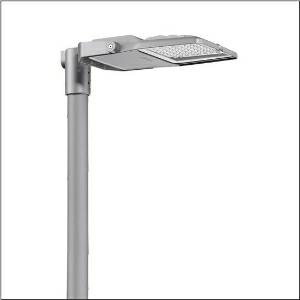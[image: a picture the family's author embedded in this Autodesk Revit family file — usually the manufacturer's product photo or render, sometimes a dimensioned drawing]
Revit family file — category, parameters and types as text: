
# Revit family: floodlight_fl_21_mini___pl52_5xa7776d2d3a_85e1
name_source: partatom
category: Lighting Fixtures
units: mm (PartAtom-declared; Revit-internal decimal feet)

## family parameters
Cut with Voids When Loaded = No
Host = Face
Light Source = No
Part Type = Normal
Room Calculation Point = No
Round Connector Dimension = Use Diameter
Shared = No

## types (1)
- --- (1 x LED, 17840 lm, 142.9 W, 3000K)
    Apparent Load = 143 VA
    CIE Flux Codes = 26 60 98 100 100
    Color Rendering = 70
    Color Temperature = 3000K
    Default Elevation = 1800 mm
    Description = Floodlight FL 21 mini, floodlight, primary light control with lens, of PMMA, primary optical cover: protective disc, of toughened safety glass, transparent, light distribution: PL52, light emission: direct distribution, installation type: surface-mounted, LED, High Power LED, rated luminous flux: 17.840lm, luminous efficacy: 125lm/W, light colour: 730, colour temperature: 3000K, control gear: Smart Interface (Zhaga), control: flexible luminous flux parameterisation, time-dependent luminous flux control, constant luminous flux control, overheat protection, pre-setting: logarithmic dimming characteristic, with terminal, 6-pole, mains connection: 220..240V, AC, 50/60Hz, start of lifetime: 143W, end of service life: 151W, reduction: 63W, luminaire housing, of diecast aluminium, powder-coated, Siteco® metallic grey (DB 702S), corrosivity category C5 mid according to DIN EN ISO 12944, suitable for swimming pools, chlorine-resistant, sealing non-destructively replaceable, please order mast flange separately, mast bracket, of steel, galvanised, powder-coated, Siteco® metallic grey (DB 702S), Smart Interface below and above, protection rating (complete): IP66, insulation class (complete): insulation class II (safety insulation), certification: CE, ENEC, VDE, protection symbol: D, impact resistance: IK08, permissible operating ambient temperature: -40..+40°C, permissible operating ambient temperature for outdoor applications: -40..+50°C, standard: DIN EN 12944, LABS conformity tested according to VDMA 24364:2018-05, packaging unit: 1 piece

Light Distribution: PL52
    Height = 70 mm
    Lamp = 1 x LED
    Lamp Light Flux = 17840 lm
    Lamp Power = 142.9 W
    Lamp count = 1
    Length = 485 mm
    Luminous efficacy = 125 lm/W
    Manufacturer = Siteco
    ModVariant = No
    Model = 5XA7776D2D3A
    Number of Poles = 1
    OnlyDefault = Yes
    Power Factor = 1
    Product Name = Floodlight FL 21 mini | PL52
    Product group = floodlight | pylon annexe
    ProductGroupID = 6201
    Protection Class = Protection class II
    Protection Degree = IP 66
    RLX_Detail_Level = 1
    RLX_Emergency_Light_Flux = 0 lm
    RLX_Emergency_Type = 0
    RLX_Emergency_Type_DB = No
    RlxData = <blob elided: 101509 chars, md5=e3d58ec7>
    Socket = socket
    Standby Power = 0 W
    System Light Flux = 17840 lm
    System Power = 143 W
    Type Comments = factory setting: luminous flux: 100 % | dim-lin: 254 | 730 mA
    Type Image = l_1007125.jpg
    URL = http://relux.com
    VarID = @adj_184563
    Voltage = 0 V
    Weight = 0.00 kg
    Width = 337 mm

## geometry (parser evidence)
native form markers: Blend x4, Sweep x11
no freeform markers — native parametric forms only
